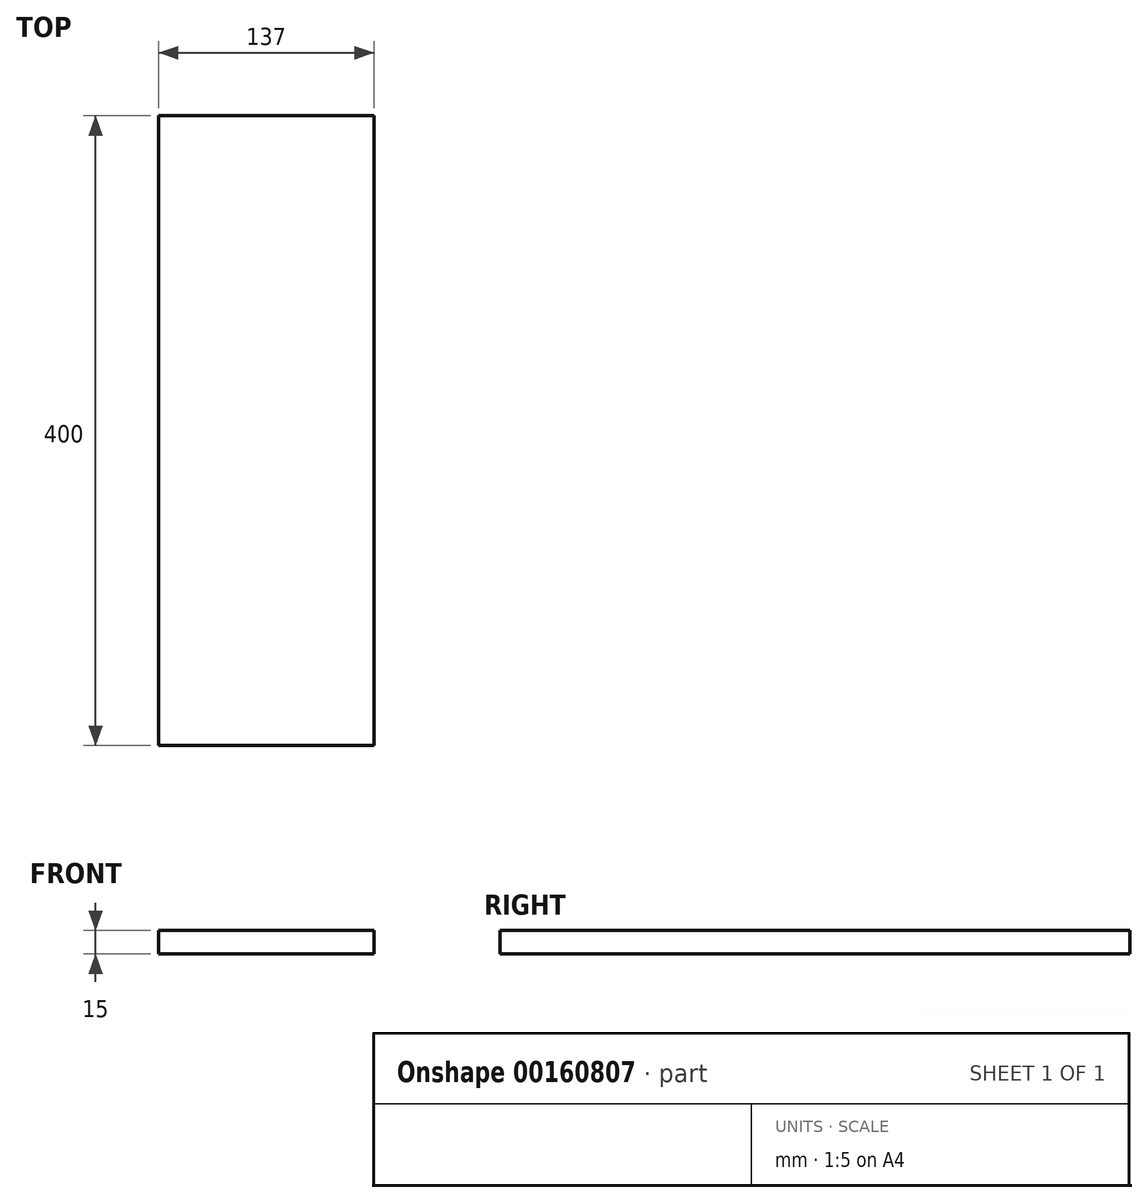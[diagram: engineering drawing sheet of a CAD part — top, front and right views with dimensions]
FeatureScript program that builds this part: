
annotation { "Feature Type Name" : "Feature", "Feature Type Description" : "" }
export const myFeature = defineFeature(function(context is Context, id is Id, definition is map)
    precondition{}
    {
        {
            var Q0;
            Q0=qCreatedBy(makeId("Front.planeOp"),FACE);
            var sketch = newSketch(context, id + "F0", { "sketchPlane" : qUnion([Q0])});
            skLineSegment(sketch, "E0.bottom", {"start": v(-146.69, 34.73) * mm, "end": v(-9.69, 34.73) * mm});
            skLineSegment(sketch, "E0.top", {"start": v(-146.69, 19.73) * mm, "end": v(-9.69, 19.73) * mm});
            skLineSegment(sketch, "E0.left", {"start": v(-146.69, 34.73) * mm, "end": v(-146.69, 19.73) * mm});
            skLineSegment(sketch, "E0.right", {"start": v(-9.69, 34.73) * mm, "end": v(-9.69, 19.73) * mm});
            skSolve(sketch);
        }
        {
            var Q0;
            Q0=makeQuery(id+"F0.imprint","IMPRINT",FACE,{"disambiguationData":[TD([[makeQuery(id+"F0.imprint","IMPRINT",EDGE,{"derivedFrom":sQuery(id+"F0.wireOp",EDGE,"E0.bottom")}),-1.0]])]});
            extrude(context, id + "F1", {"entities" : qUnion([Q0]), "depth" : 400 * mm});
        }
    });
